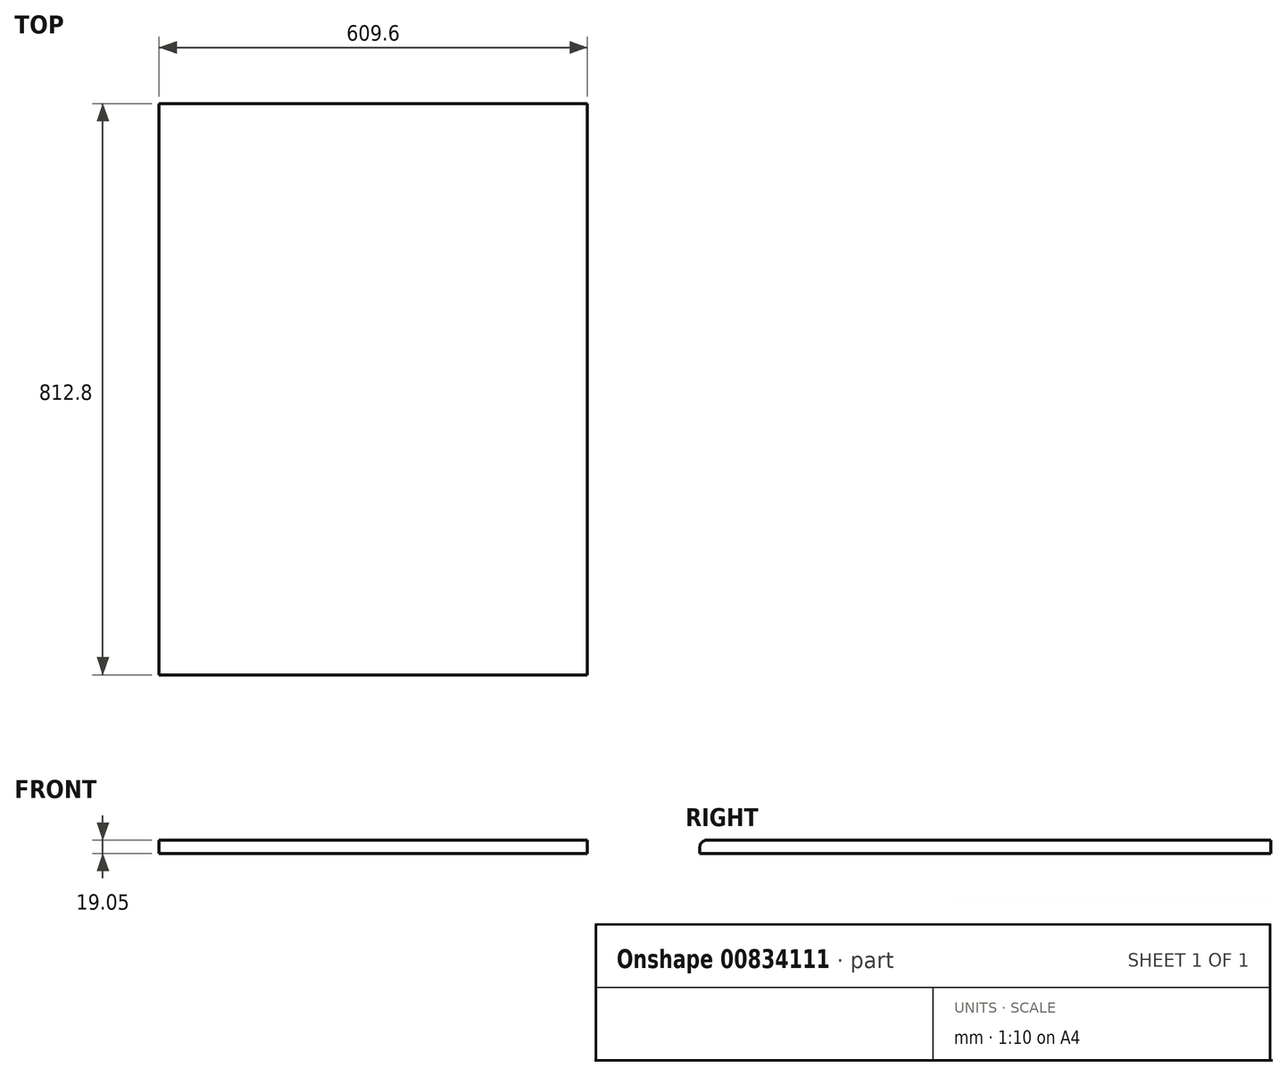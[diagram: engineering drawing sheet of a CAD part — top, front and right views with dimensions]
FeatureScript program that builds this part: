
annotation { "Feature Type Name" : "Feature", "Feature Type Description" : "" }
export const myFeature = defineFeature(function(context is Context, id is Id, definition is map)
    precondition{}
    {
        {
            var Q0;
            Q0=qCreatedBy(makeId("Top.planeOp"),FACE);
            var sketch = newSketch(context, id + "F0", { "sketchPlane" : qUnion([Q0])});
            skLineSegment(sketch, "E0.bottom", {"start": v(304.8, -406.4) * mm, "end": v(-304.8, -406.4) * mm});
            skLineSegment(sketch, "E0.top", {"start": v(304.8, 406.4) * mm, "end": v(-304.8, 406.4) * mm});
            skLineSegment(sketch, "E0.left", {"start": v(304.8, -406.4) * mm, "end": v(304.8, 406.4) * mm});
            skLineSegment(sketch, "E0.right", {"start": v(-304.8, -406.4) * mm, "end": v(-304.8, 406.4) * mm});
            skPoint(sketch, "E0.middle", {"position": v(0, 0) * mm});
            skSolve(sketch);
        }
        {
            var Q0;
            Q0=qSketchRegion(id+"F0",true);
            extrude(context, id + "F1", {"entities" : qUnion([Q0]), "depth" : 19.05 * mm});
        }
        {
            var Q0;
            Q0=makeQuery(id+"F1.opExtrude","CAP_EDGE",EDGE,{"disambiguationData":[OSD([sQuery(id+"F0.wireOp",EDGE,"E0.bottom")])],"isStart":false});
            fillet(context, id + "F2", {"entities" : qUnion([Q0]), "radius" : 10.16 * mm, "tangentPropagation" : true, "allowEdgeOverflow" : false});
        }
    });
